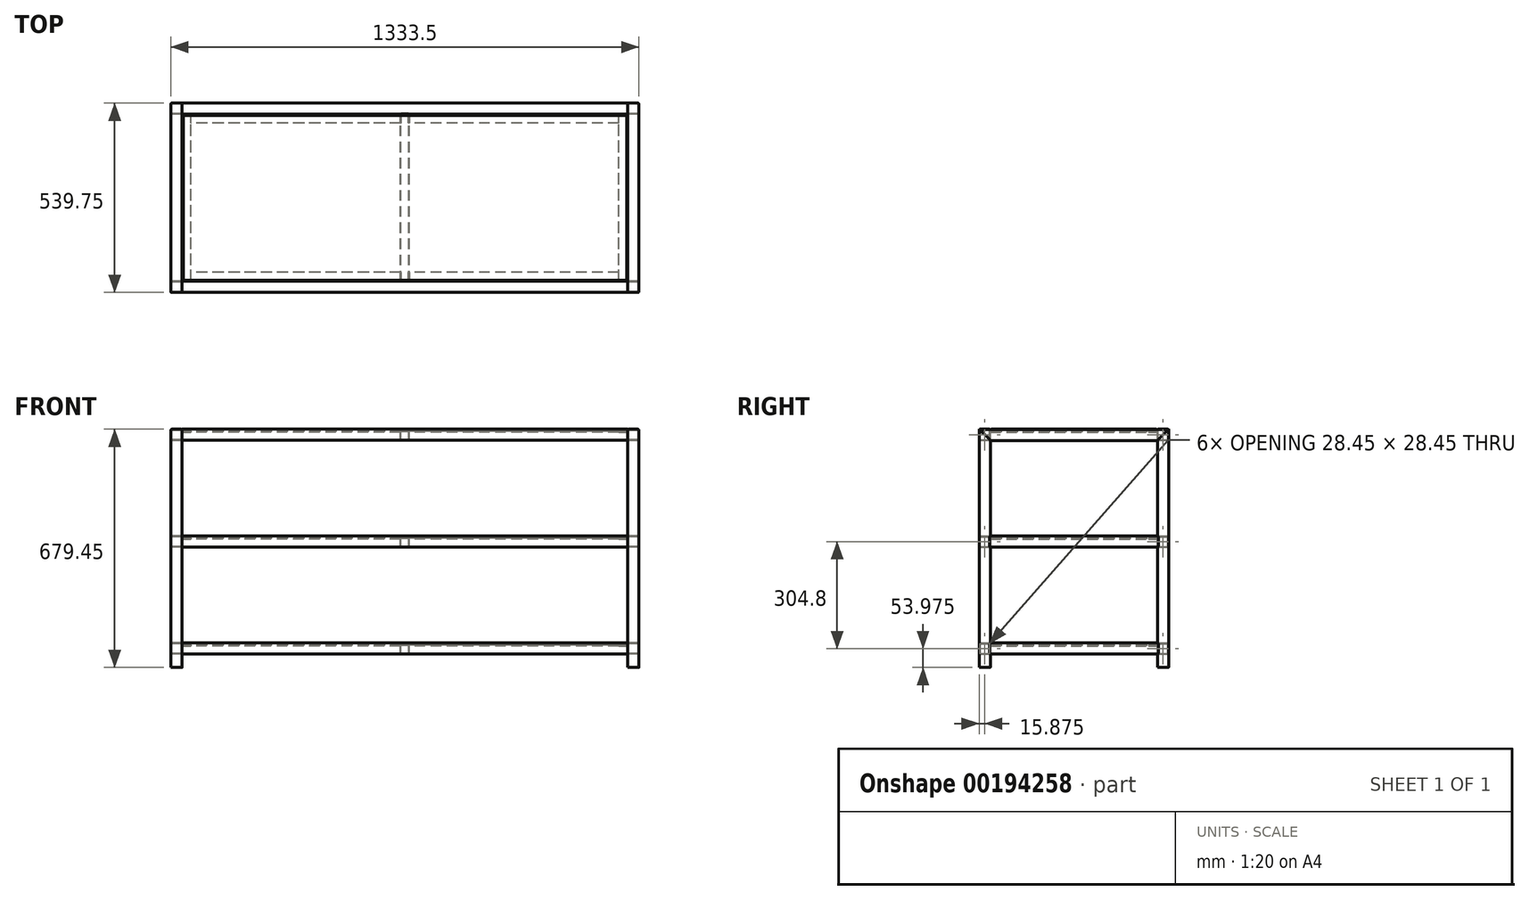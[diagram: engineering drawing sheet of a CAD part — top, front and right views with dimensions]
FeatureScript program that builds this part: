
annotation { "Feature Type Name" : "Feature", "Feature Type Description" : "" }
export const myFeature = defineFeature(function(context is Context, id is Id, definition is map)
    precondition{}
    {
        {
            var Q0;
            Q0=qCreatedBy(makeId("Right.planeOp"),FACE);
            var sketch = newSketch(context, id + "F0", { "sketchPlane" : qUnion([Q0])});
            skLineSegment(sketch, "E0.bottom", {"start": v(2.54, 0) * mm, "end": v(29.21, 0) * mm});
            skLineSegment(sketch, "E0.top", {"start": v(2.54, 31.75) * mm, "end": v(29.21, 31.75) * mm});
            skLineSegment(sketch, "E0.left", {"start": v(0, 2.54) * mm, "end": v(0, 29.21) * mm});
            skLineSegment(sketch, "E0.right", {"start": v(31.75, 2.54) * mm, "end": v(31.75, 29.21) * mm});
            skPoint(sketch, "E1.visualSharp", {"position": v(0, 31.75) * mm});
            skArc(sketch, "E1.filletArc", {"start": v(2.54, 31.75) * mm, "mid": v(0.74, 31) * mm, "end": v(0, 29.21) * mm});
            skPoint(sketch, "E2.visualSharp", {"position": v(31.75, 31.75) * mm});
            skArc(sketch, "E2.filletArc", {"start": v(31.75, 29.21) * mm, "mid": v(31, 31) * mm, "end": v(29.21, 31.75) * mm});
            skPoint(sketch, "E3.visualSharp", {"position": v(31.75, 0) * mm});
            skArc(sketch, "E3.filletArc", {"start": v(29.21, 0) * mm, "mid": v(31, 0.74) * mm, "end": v(31.75, 2.54) * mm});
            skPoint(sketch, "E4.visualSharp", {"position": v(0, 0) * mm});
            skArc(sketch, "E4.filletArc", {"start": v(0, 2.54) * mm, "mid": v(0.74, 0.74) * mm, "end": v(2.54, 0) * mm});
            skLineSegment(sketch, "E5.0", {"start": v(2.54, 30.1) * mm, "end": v(29.21, 30.1) * mm});
            skArc(sketch, "E5.1", {"start": v(2.54, 30.1) * mm, "mid": v(1.91, 29.84) * mm, "end": v(1.65, 29.21) * mm});
            skLineSegment(sketch, "E5.2", {"start": v(1.65, 2.54) * mm, "end": v(1.65, 29.21) * mm});
            skLineSegment(sketch, "E5.3", {"start": v(30.1, 2.54) * mm, "end": v(30.1, 29.21) * mm});
            skArc(sketch, "E5.4", {"start": v(29.21, 1.65) * mm, "mid": v(29.84, 1.91) * mm, "end": v(30.1, 2.54) * mm});
            skLineSegment(sketch, "E5.5", {"start": v(2.54, 1.65) * mm, "end": v(29.21, 1.65) * mm});
            skArc(sketch, "E5.6", {"start": v(1.65, 2.54) * mm, "mid": v(1.91, 1.91) * mm, "end": v(2.54, 1.65) * mm});
            skArc(sketch, "E6.0", {"start": v(30.1, 29.21) * mm, "mid": v(29.84, 29.84) * mm, "end": v(29.21, 30.1) * mm});
            skSolve(sketch);
        }
        {
            var Q0;
            Q0 = qSketchRegion(id + "F0", true);
            extrude(context, id + "F1", {"entities" : qUnion([Q0]), "depth" : 1270 * mm});
        }
        {
            var Q0;
            Q0=makeQuery(id+"F1.opExtrude","SWEPT_BODY",BODY,{"disambiguationData":[OSD([sQuery(id+"F0.wireOp",EDGE,"E0.bottom"),sQuery(id+"F0.wireOp",EDGE,"E0.top"),sQuery(id+"F0.wireOp",EDGE,"E0.left"),sQuery(id+"F0.wireOp",EDGE,"E0.right"),sQuery(id+"F0.wireOp",EDGE,"E1.filletArc"),sQuery(id+"F0.wireOp",EDGE,"E2.filletArc"),sQuery(id+"F0.wireOp",EDGE,"E3.filletArc"),sQuery(id+"F0.wireOp",EDGE,"E4.filletArc"),sQuery(id+"F0.wireOp",EDGE,"E5.0"),sQuery(id+"F0.wireOp",EDGE,"E5.1"),sQuery(id+"F0.wireOp",EDGE,"E5.2"),sQuery(id+"F0.wireOp",EDGE,"E5.3"),sQuery(id+"F0.wireOp",EDGE,"E5.4"),sQuery(id+"F0.wireOp",EDGE,"E5.5"),sQuery(id+"F0.wireOp",EDGE,"E5.6"),sQuery(id+"F0.wireOp",EDGE,"E6.0")])]});
            transform(context, id + "F2", {"entities" : qUnion([Q0]), "transformType" : TransformType.TRANSLATION_3D, "dx" : 0 * mm, "dy" : 0 * mm, "dz" : 304.8 * mm, "makeCopy" : true});
        }
        {
            var Q0;
            Q0=makeQuery(id+"F2.opPattern","COPY",BODY,{"derivedFrom":makeQuery(id+"F1.opExtrude","SWEPT_BODY",BODY,{"disambiguationData":[OSD([sQuery(id+"F0.wireOp",EDGE,"E0.bottom"),sQuery(id+"F0.wireOp",EDGE,"E0.top"),sQuery(id+"F0.wireOp",EDGE,"E0.left"),sQuery(id+"F0.wireOp",EDGE,"E0.right"),sQuery(id+"F0.wireOp",EDGE,"E1.filletArc"),sQuery(id+"F0.wireOp",EDGE,"E2.filletArc"),sQuery(id+"F0.wireOp",EDGE,"E3.filletArc"),sQuery(id+"F0.wireOp",EDGE,"E4.filletArc"),sQuery(id+"F0.wireOp",EDGE,"E5.0"),sQuery(id+"F0.wireOp",EDGE,"E5.1"),sQuery(id+"F0.wireOp",EDGE,"E5.2"),sQuery(id+"F0.wireOp",EDGE,"E5.3"),sQuery(id+"F0.wireOp",EDGE,"E5.4"),sQuery(id+"F0.wireOp",EDGE,"E5.5"),sQuery(id+"F0.wireOp",EDGE,"E5.6"),sQuery(id+"F0.wireOp",EDGE,"E6.0")])]}),"instanceName":"1"});
            transform(context, id + "F3", {"entities" : qUnion([Q0]), "transformType" : TransformType.TRANSLATION_3D, "dx" : 0 * mm, "dy" : 0 * mm, "dz" : 304.8 * mm, "makeCopy" : true});
        }
        {
            var Q0;
            Q0=makeQuery(id+"F1.opExtrude","SWEPT_BODY",BODY,{"disambiguationData":[OSD([sQuery(id+"F0.wireOp",EDGE,"E0.bottom"),sQuery(id+"F0.wireOp",EDGE,"E0.top"),sQuery(id+"F0.wireOp",EDGE,"E0.left"),sQuery(id+"F0.wireOp",EDGE,"E0.right"),sQuery(id+"F0.wireOp",EDGE,"E1.filletArc"),sQuery(id+"F0.wireOp",EDGE,"E2.filletArc"),sQuery(id+"F0.wireOp",EDGE,"E3.filletArc"),sQuery(id+"F0.wireOp",EDGE,"E4.filletArc"),sQuery(id+"F0.wireOp",EDGE,"E5.0"),sQuery(id+"F0.wireOp",EDGE,"E5.1"),sQuery(id+"F0.wireOp",EDGE,"E5.2"),sQuery(id+"F0.wireOp",EDGE,"E5.3"),sQuery(id+"F0.wireOp",EDGE,"E5.4"),sQuery(id+"F0.wireOp",EDGE,"E5.5"),sQuery(id+"F0.wireOp",EDGE,"E5.6"),sQuery(id+"F0.wireOp",EDGE,"E6.0")])]});
            transform(context, id + "F4", {"entities" : qUnion([Q0]), "transformType" : TransformType.TRANSLATION_3D, "dx" : 0 * mm, "dy" : 508 * mm, "dz" : 0 * mm, "makeCopy" : true});
        }
        {
            var Q0;
            Q0=makeQuery(id+"F4.opPattern","COPY",BODY,{"derivedFrom":makeQuery(id+"F1.opExtrude","SWEPT_BODY",BODY,{"disambiguationData":[OSD([sQuery(id+"F0.wireOp",EDGE,"E0.bottom"),sQuery(id+"F0.wireOp",EDGE,"E0.top"),sQuery(id+"F0.wireOp",EDGE,"E0.left"),sQuery(id+"F0.wireOp",EDGE,"E0.right"),sQuery(id+"F0.wireOp",EDGE,"E1.filletArc"),sQuery(id+"F0.wireOp",EDGE,"E2.filletArc"),sQuery(id+"F0.wireOp",EDGE,"E3.filletArc"),sQuery(id+"F0.wireOp",EDGE,"E4.filletArc"),sQuery(id+"F0.wireOp",EDGE,"E5.0"),sQuery(id+"F0.wireOp",EDGE,"E5.1"),sQuery(id+"F0.wireOp",EDGE,"E5.2"),sQuery(id+"F0.wireOp",EDGE,"E5.3"),sQuery(id+"F0.wireOp",EDGE,"E5.4"),sQuery(id+"F0.wireOp",EDGE,"E5.5"),sQuery(id+"F0.wireOp",EDGE,"E5.6"),sQuery(id+"F0.wireOp",EDGE,"E6.0")])]}),"instanceName":"1"});
            transform(context, id + "F5", {"entities" : qUnion([Q0]), "transformType" : TransformType.TRANSLATION_3D, "dx" : 0 * mm, "dy" : 0 * mm, "dz" : 304.8 * mm, "makeCopy" : true});
        }
        {
            var Q0;
            Q0=makeQuery(id+"F5.opPattern","COPY",BODY,{"derivedFrom":makeQuery(id+"F4.opPattern","COPY",BODY,{"derivedFrom":makeQuery(id+"F1.opExtrude","SWEPT_BODY",BODY,{"disambiguationData":[OSD([sQuery(id+"F0.wireOp",EDGE,"E0.bottom"),sQuery(id+"F0.wireOp",EDGE,"E0.top"),sQuery(id+"F0.wireOp",EDGE,"E0.left"),sQuery(id+"F0.wireOp",EDGE,"E0.right"),sQuery(id+"F0.wireOp",EDGE,"E1.filletArc"),sQuery(id+"F0.wireOp",EDGE,"E2.filletArc"),sQuery(id+"F0.wireOp",EDGE,"E3.filletArc"),sQuery(id+"F0.wireOp",EDGE,"E4.filletArc"),sQuery(id+"F0.wireOp",EDGE,"E5.0"),sQuery(id+"F0.wireOp",EDGE,"E5.1"),sQuery(id+"F0.wireOp",EDGE,"E5.2"),sQuery(id+"F0.wireOp",EDGE,"E5.3"),sQuery(id+"F0.wireOp",EDGE,"E5.4"),sQuery(id+"F0.wireOp",EDGE,"E5.5"),sQuery(id+"F0.wireOp",EDGE,"E5.6"),sQuery(id+"F0.wireOp",EDGE,"E6.0")])]}),"instanceName":"1"}),"instanceName":"1"});
            transform(context, id + "F6", {"entities" : qUnion([Q0]), "transformType" : TransformType.TRANSLATION_3D, "dx" : 0 * mm, "dy" : 0 * mm, "dz" : 304.8 * mm, "makeCopy" : true});
        }
        {
            var Q0;
            Q0=qCreatedBy(makeId("Top.planeOp"),FACE);
            var sketch = newSketch(context, id + "F7", { "sketchPlane" : qUnion([Q0])});
            skLineSegment(sketch, "E7.bottom", {"start": v(-2.54, 0) * mm, "end": v(-29.21, 0) * mm});
            skLineSegment(sketch, "E7.top", {"start": v(-2.54, 31.75) * mm, "end": v(-29.21, 31.75) * mm});
            skLineSegment(sketch, "E7.left", {"start": v(0, 2.54) * mm, "end": v(0, 29.21) * mm});
            skLineSegment(sketch, "E7.right", {"start": v(-31.75, 2.54) * mm, "end": v(-31.75, 29.21) * mm});
            skPoint(sketch, "E8.visualSharp", {"position": v(-31.75, 31.75) * mm});
            skArc(sketch, "E8.filletArc", {"start": v(-29.21, 31.75) * mm, "mid": v(-31, 31) * mm, "end": v(-31.75, 29.21) * mm});
            skPoint(sketch, "E9.visualSharp", {"position": v(0, 31.75) * mm});
            skArc(sketch, "E9.filletArc", {"start": v(0, 29.21) * mm, "mid": v(-0.74, 31) * mm, "end": v(-2.54, 31.75) * mm});
            skPoint(sketch, "E10.visualSharp", {"position": v(0, 0) * mm});
            skArc(sketch, "E10.filletArc", {"start": v(-2.54, 0) * mm, "mid": v(-0.74, 0.74) * mm, "end": v(0, 2.54) * mm});
            skPoint(sketch, "E11.visualSharp", {"position": v(-31.75, 0) * mm});
            skArc(sketch, "E11.filletArc", {"start": v(-31.75, 2.54) * mm, "mid": v(-31, 0.74) * mm, "end": v(-29.21, 0) * mm});
            skArc(sketch, "E12.0", {"start": v(-1.65, 29.21) * mm, "mid": v(-1.91, 29.84) * mm, "end": v(-2.54, 30.1) * mm});
            skLineSegment(sketch, "E12.1", {"start": v(-1.65, 2.54) * mm, "end": v(-1.65, 29.21) * mm});
            skLineSegment(sketch, "E12.2", {"start": v(-2.54, 30.1) * mm, "end": v(-29.21, 30.1) * mm});
            skArc(sketch, "E12.3", {"start": v(-2.54, 1.65) * mm, "mid": v(-1.91, 1.91) * mm, "end": v(-1.65, 2.54) * mm});
            skArc(sketch, "E12.4", {"start": v(-29.21, 30.1) * mm, "mid": v(-29.84, 29.84) * mm, "end": v(-30.1, 29.21) * mm});
            skLineSegment(sketch, "E12.5", {"start": v(-30.1, 2.54) * mm, "end": v(-30.1, 29.21) * mm});
            skArc(sketch, "E12.6", {"start": v(-30.1, 2.54) * mm, "mid": v(-29.84, 1.91) * mm, "end": v(-29.21, 1.65) * mm});
            skLineSegment(sketch, "E12.7", {"start": v(-2.54, 1.65) * mm, "end": v(-29.21, 1.65) * mm});
            skSolve(sketch);
        }
        {
            var Q0;
            Q0 = qSketchRegion(id + "F7", true);
            var Q1;
            Q1=makeQuery(id+"F3.opPattern","COPY",FACE,{"derivedFrom":makeQuery(id+"F2.opPattern","COPY",FACE,{"derivedFrom":makeQuery(id+"F1.opExtrude","SWEPT_FACE",FACE,{"disambiguationData":[OSD([sQuery(id+"F0.wireOp",EDGE,"E0.top")])]}),"instanceName":"1"}),"instanceName":"1"});
            extrude(context, id + "F8", {"entities" : qUnion([Q0]), "endBound" : BoundingType.UP_TO_SURFACE, "endBoundEntityFace" : qUnion([Q1]), "depth" : 25.4 * mm, "hasSecondDirection" : true, "secondDirectionOppositeDirection" : true, "secondDirectionDepth" : 38.1 * mm});
        }
        {
            var Q0;
            Q0=makeQuery(id+"F8.opExtrude","SWEPT_BODY",BODY,{"disambiguationData":[OSD([sQuery(id+"F7.wireOp",EDGE,"E7.bottom"),sQuery(id+"F7.wireOp",EDGE,"E7.top"),sQuery(id+"F7.wireOp",EDGE,"E7.left"),sQuery(id+"F7.wireOp",EDGE,"E7.right"),sQuery(id+"F7.wireOp",EDGE,"E8.filletArc"),sQuery(id+"F7.wireOp",EDGE,"E9.filletArc"),sQuery(id+"F7.wireOp",EDGE,"E10.filletArc"),sQuery(id+"F7.wireOp",EDGE,"E11.filletArc"),sQuery(id+"F7.wireOp",EDGE,"E12.0"),sQuery(id+"F7.wireOp",EDGE,"E12.1"),sQuery(id+"F7.wireOp",EDGE,"E12.2"),sQuery(id+"F7.wireOp",EDGE,"E12.3"),sQuery(id+"F7.wireOp",EDGE,"E12.4"),sQuery(id+"F7.wireOp",EDGE,"E12.5"),sQuery(id+"F7.wireOp",EDGE,"E12.6"),sQuery(id+"F7.wireOp",EDGE,"E12.7")])]});
            transform(context, id + "F9", {"entities" : qUnion([Q0]), "transformType" : TransformType.TRANSLATION_3D, "dx" : 1301.75 * mm, "dy" : 0 * mm, "dz" : 0 * mm, "makeCopy" : true});
        }
        {
            var Q0;
            Q0=makeQuery(id+"F8.opExtrude","SWEPT_FACE",FACE,{"disambiguationData":[OSD([sQuery(id+"F7.wireOp",EDGE,"E7.right")])]});
            var sketch = newSketch(context, id + "F10", { "sketchPlane" : qUnion([Q0])});
            skLineSegment(sketch, "E13.bottom", {"start": v(0, 641.35) * mm, "end": v(-31.75, 641.35) * mm});
            skLineSegment(sketch, "E13.right", {"start": v(-31.75, 641.35) * mm, "end": v(-31.75, 609.6) * mm});
            skLineSegment(sketch, "E14", {"start": v(-31.75, 609.6) * mm, "end": v(0, 641.35) * mm});
            skSolve(sketch);
        }
        {
            var Q0;
            Q0 = qSketchRegion(id + "F10", true);
            extrude(context, id + "F11", {"entities" : qUnion([Q0]), "operationType" : NewBodyOperationType.REMOVE, "oppositeDirection" : true, "depth" : 31.75 * mm});
        }
        {
            var Q0;
            Q0=makeQuery(id+"F9.opPattern","COPY",BODY,{"derivedFrom":makeQuery(id+"F8.opExtrude","SWEPT_BODY",BODY,{"disambiguationData":[OSD([sQuery(id+"F7.wireOp",EDGE,"E7.bottom"),sQuery(id+"F7.wireOp",EDGE,"E7.top"),sQuery(id+"F7.wireOp",EDGE,"E7.left"),sQuery(id+"F7.wireOp",EDGE,"E7.right"),sQuery(id+"F7.wireOp",EDGE,"E8.filletArc"),sQuery(id+"F7.wireOp",EDGE,"E9.filletArc"),sQuery(id+"F7.wireOp",EDGE,"E10.filletArc"),sQuery(id+"F7.wireOp",EDGE,"E11.filletArc"),sQuery(id+"F7.wireOp",EDGE,"E12.0"),sQuery(id+"F7.wireOp",EDGE,"E12.1"),sQuery(id+"F7.wireOp",EDGE,"E12.2"),sQuery(id+"F7.wireOp",EDGE,"E12.3"),sQuery(id+"F7.wireOp",EDGE,"E12.4"),sQuery(id+"F7.wireOp",EDGE,"E12.5"),sQuery(id+"F7.wireOp",EDGE,"E12.6"),sQuery(id+"F7.wireOp",EDGE,"E12.7")])]}),"instanceName":"1"});
            deleteBodies(context, id + "F12", {"entities" : qUnion([Q0])});
        }
        {
            var Q0;
            Q0=makeQuery(id+"F8.opExtrude","SWEPT_BODY",BODY,{"disambiguationData":[OSD([sQuery(id+"F7.wireOp",EDGE,"E7.bottom"),sQuery(id+"F7.wireOp",EDGE,"E7.top"),sQuery(id+"F7.wireOp",EDGE,"E7.left"),sQuery(id+"F7.wireOp",EDGE,"E7.right"),sQuery(id+"F7.wireOp",EDGE,"E8.filletArc"),sQuery(id+"F7.wireOp",EDGE,"E9.filletArc"),sQuery(id+"F7.wireOp",EDGE,"E10.filletArc"),sQuery(id+"F7.wireOp",EDGE,"E11.filletArc"),sQuery(id+"F7.wireOp",EDGE,"E12.0"),sQuery(id+"F7.wireOp",EDGE,"E12.1"),sQuery(id+"F7.wireOp",EDGE,"E12.2"),sQuery(id+"F7.wireOp",EDGE,"E12.3"),sQuery(id+"F7.wireOp",EDGE,"E12.4"),sQuery(id+"F7.wireOp",EDGE,"E12.5"),sQuery(id+"F7.wireOp",EDGE,"E12.6"),sQuery(id+"F7.wireOp",EDGE,"E12.7")])]});
            transform(context, id + "F13", {"entities" : qUnion([Q0]), "transformType" : TransformType.TRANSLATION_3D, "dx" : 1301.75 * mm, "dy" : 0 * mm, "dz" : 0 * mm, "makeCopy" : true});
        }
        {
            var Q0;
            Q0=makeQuery(id+"F8.opExtrude","SWEPT_BODY",BODY,{"disambiguationData":[OSD([sQuery(id+"F7.wireOp",EDGE,"E7.bottom"),sQuery(id+"F7.wireOp",EDGE,"E7.top"),sQuery(id+"F7.wireOp",EDGE,"E7.left"),sQuery(id+"F7.wireOp",EDGE,"E7.right"),sQuery(id+"F7.wireOp",EDGE,"E8.filletArc"),sQuery(id+"F7.wireOp",EDGE,"E9.filletArc"),sQuery(id+"F7.wireOp",EDGE,"E10.filletArc"),sQuery(id+"F7.wireOp",EDGE,"E11.filletArc"),sQuery(id+"F7.wireOp",EDGE,"E12.0"),sQuery(id+"F7.wireOp",EDGE,"E12.1"),sQuery(id+"F7.wireOp",EDGE,"E12.2"),sQuery(id+"F7.wireOp",EDGE,"E12.3"),sQuery(id+"F7.wireOp",EDGE,"E12.4"),sQuery(id+"F7.wireOp",EDGE,"E12.5"),sQuery(id+"F7.wireOp",EDGE,"E12.6"),sQuery(id+"F7.wireOp",EDGE,"E12.7")])]});
            transform(context, id + "F14", {"entities" : qUnion([Q0]), "transformType" : TransformType.TRANSLATION_3D, "dx" : 0 * mm, "dy" : 508 * mm, "dz" : 0 * mm, "makeCopy" : true});
        }
        {
            var Q0;
            Q0=makeQuery(id+"F14.opPattern","COPY",BODY,{"derivedFrom":makeQuery(id+"F8.opExtrude","SWEPT_BODY",BODY,{"disambiguationData":[OSD([sQuery(id+"F7.wireOp",EDGE,"E7.bottom"),sQuery(id+"F7.wireOp",EDGE,"E7.top"),sQuery(id+"F7.wireOp",EDGE,"E7.left"),sQuery(id+"F7.wireOp",EDGE,"E7.right"),sQuery(id+"F7.wireOp",EDGE,"E8.filletArc"),sQuery(id+"F7.wireOp",EDGE,"E9.filletArc"),sQuery(id+"F7.wireOp",EDGE,"E10.filletArc"),sQuery(id+"F7.wireOp",EDGE,"E11.filletArc"),sQuery(id+"F7.wireOp",EDGE,"E12.0"),sQuery(id+"F7.wireOp",EDGE,"E12.1"),sQuery(id+"F7.wireOp",EDGE,"E12.2"),sQuery(id+"F7.wireOp",EDGE,"E12.3"),sQuery(id+"F7.wireOp",EDGE,"E12.4"),sQuery(id+"F7.wireOp",EDGE,"E12.5"),sQuery(id+"F7.wireOp",EDGE,"E12.6"),sQuery(id+"F7.wireOp",EDGE,"E12.7")])]}),"instanceName":"1"});
            deleteBodies(context, id + "F15", {"entities" : qUnion([Q0])});
        }
        {
            var Q0;
            Q0=qCreatedBy(makeId("Top.planeOp"),FACE);
            var sketch = newSketch(context, id + "F16", { "sketchPlane" : qUnion([Q0])});
            skLineSegment(sketch, "E15.bottom", {"start": v(-2.54, 508) * mm, "end": v(-29.21, 508) * mm});
            skLineSegment(sketch, "E15.top", {"start": v(-2.54, 539.75) * mm, "end": v(-29.21, 539.75) * mm});
            skLineSegment(sketch, "E15.left", {"start": v(0, 510.54) * mm, "end": v(0, 537.2) * mm});
            skLineSegment(sketch, "E15.right", {"start": v(-31.75, 510.54) * mm, "end": v(-31.75, 537.2) * mm});
            skPoint(sketch, "E16.visualSharp", {"position": v(-31.75, 539.75) * mm});
            skArc(sketch, "E16.filletArc", {"start": v(-29.21, 539.75) * mm, "mid": v(-31, 539) * mm, "end": v(-31.75, 537.2) * mm});
            skPoint(sketch, "E17.visualSharp", {"position": v(0, 539.75) * mm});
            skArc(sketch, "E17.filletArc", {"start": v(0, 537.2) * mm, "mid": v(-0.74, 539) * mm, "end": v(-2.54, 539.75) * mm});
            skPoint(sketch, "E18.visualSharp", {"position": v(0, 508) * mm});
            skArc(sketch, "E18.filletArc", {"start": v(-2.54, 508) * mm, "mid": v(-0.74, 508.74) * mm, "end": v(0, 510.54) * mm});
            skPoint(sketch, "E19.visualSharp", {"position": v(-31.75, 508) * mm});
            skArc(sketch, "E19.filletArc", {"start": v(-31.75, 510.54) * mm, "mid": v(-31, 508.74) * mm, "end": v(-29.21, 508) * mm});
            skArc(sketch, "E20.0", {"start": v(-1.65, 537.2) * mm, "mid": v(-1.91, 537.84) * mm, "end": v(-2.54, 538.1) * mm});
            skLineSegment(sketch, "E20.1", {"start": v(-1.65, 510.54) * mm, "end": v(-1.65, 537.2) * mm});
            skLineSegment(sketch, "E20.2", {"start": v(-2.54, 538.1) * mm, "end": v(-29.21, 538.1) * mm});
            skArc(sketch, "E20.3", {"start": v(-2.54, 509.65) * mm, "mid": v(-1.91, 509.91) * mm, "end": v(-1.65, 510.54) * mm});
            skArc(sketch, "E20.4", {"start": v(-29.21, 538.1) * mm, "mid": v(-29.84, 537.84) * mm, "end": v(-30.1, 537.2) * mm});
            skLineSegment(sketch, "E20.5", {"start": v(-30.1, 510.54) * mm, "end": v(-30.1, 537.2) * mm});
            skArc(sketch, "E20.6", {"start": v(-30.1, 510.54) * mm, "mid": v(-29.84, 509.91) * mm, "end": v(-29.21, 509.65) * mm});
            skLineSegment(sketch, "E20.7", {"start": v(-2.54, 509.65) * mm, "end": v(-29.21, 509.65) * mm});
            skSolve(sketch);
        }
        {
            var Q0;
            Q0=makeQuery(id+"F16.imprint","IMPRINT",FACE,{"disambiguationData":[TD([[makeQuery(id+"F16.imprint","IMPRINT",EDGE,{"derivedFrom":sQuery(id+"F16.wireOp",EDGE,"E15.bottom")}),-1.0]])]});
            var Q1;
            Q1=makeQuery(id+"F6.opPattern","COPY",FACE,{"derivedFrom":makeQuery(id+"F5.opPattern","COPY",FACE,{"derivedFrom":makeQuery(id+"F4.opPattern","COPY",FACE,{"derivedFrom":makeQuery(id+"F1.opExtrude","SWEPT_FACE",FACE,{"disambiguationData":[OSD([sQuery(id+"F0.wireOp",EDGE,"E0.top")])]}),"instanceName":"1"}),"instanceName":"1"}),"instanceName":"1"});
            extrude(context, id + "F17", {"entities" : qUnion([Q0]), "endBound" : BoundingType.UP_TO_SURFACE, "endBoundEntityFace" : qUnion([Q1]), "depth" : 25.4 * mm, "hasSecondDirection" : true, "secondDirectionOppositeDirection" : true, "secondDirectionDepth" : 38.1 * mm});
        }
        {
            var Q0;
            Q0=makeQuery(id+"F17.opExtrude","SWEPT_FACE",FACE,{"disambiguationData":[OSD([sQuery(id+"F16.wireOp",EDGE,"E15.right")])]});
            var sketch = newSketch(context, id + "F18", { "sketchPlane" : qUnion([Q0])});
            skLineSegment(sketch, "E21.bottom", {"start": v(-508, 641.35) * mm, "end": v(-539.75, 641.35) * mm});
            skLineSegment(sketch, "E21.left", {"start": v(-508, 641.35) * mm, "end": v(-508, 609.6) * mm});
            skLineSegment(sketch, "E22", {"start": v(-539.75, 641.35) * mm, "end": v(-508, 609.6) * mm});
            skSolve(sketch);
        }
        {
            var Q0;
            Q0 = qSketchRegion(id + "F18", true);
            extrude(context, id + "F19", {"entities" : qUnion([Q0]), "operationType" : NewBodyOperationType.REMOVE, "oppositeDirection" : true, "depth" : 31.75 * mm});
        }
        {
            var Q0;
            Q0=makeQuery(id+"F17.opExtrude","SWEPT_BODY",BODY,{"disambiguationData":[OSD([sQuery(id+"F16.wireOp",EDGE,"E15.bottom"),sQuery(id+"F16.wireOp",EDGE,"E15.top"),sQuery(id+"F16.wireOp",EDGE,"E15.left"),sQuery(id+"F16.wireOp",EDGE,"E15.right"),sQuery(id+"F16.wireOp",EDGE,"E16.filletArc"),sQuery(id+"F16.wireOp",EDGE,"E17.filletArc"),sQuery(id+"F16.wireOp",EDGE,"E18.filletArc"),sQuery(id+"F16.wireOp",EDGE,"E19.filletArc"),sQuery(id+"F16.wireOp",EDGE,"E20.0"),sQuery(id+"F16.wireOp",EDGE,"E20.1"),sQuery(id+"F16.wireOp",EDGE,"E20.2"),sQuery(id+"F16.wireOp",EDGE,"E20.3"),sQuery(id+"F16.wireOp",EDGE,"E20.4"),sQuery(id+"F16.wireOp",EDGE,"E20.5"),sQuery(id+"F16.wireOp",EDGE,"E20.6"),sQuery(id+"F16.wireOp",EDGE,"E20.7")])]});
            transform(context, id + "F20", {"entities" : qUnion([Q0]), "transformType" : TransformType.TRANSLATION_3D, "dx" : 1301.75 * mm, "dy" : 0 * mm, "dz" : 0 * mm, "makeCopy" : true});
        }
        {
            var Q0;
            Q0=qCreatedBy(makeId("Front.planeOp"),FACE);
            cPlane(context, id + "F21", {"entities" : qUnion([Q0]), "cplaneType" : CPlaneType.OFFSET, "offset" : 279.4 * mm, "oppositeDirection" : true, "width" : 152.4 * mm, "height" : 152.4 * mm});
        }
        {
            var Q0;
            Q0=qCreatedBy(id+"F21.planeOp",FACE);
            var sketch = newSketch(context, id + "F22", { "sketchPlane" : qUnion([Q0])});
            skLineSegment(sketch, "E23.0", {"start": v(-2.54, 641.35) * mm, "end": v(-29.2, 641.35) * mm});
            skPoint(sketch, "E24.0", {"position": v(-31.75, 625.47) * mm});
            skLineSegment(sketch, "E25.bottom", {"start": v(-2.54, 641.26) * mm, "end": v(-29.21, 641.26) * mm});
            skLineSegment(sketch, "E25.top", {"start": v(-2.54, 609.51) * mm, "end": v(-29.21, 609.51) * mm});
            skLineSegment(sketch, "E25.left", {"start": v(0, 638.72) * mm, "end": v(0, 612.05) * mm});
            skLineSegment(sketch, "E25.right", {"start": v(-31.75, 638.72) * mm, "end": v(-31.75, 612.05) * mm});
            skPoint(sketch, "E26.visualSharp", {"position": v(0, 641.26) * mm});
            skArc(sketch, "E26.filletArc", {"start": v(0, 638.72) * mm, "mid": v(-0.74, 640.52) * mm, "end": v(-2.54, 641.26) * mm});
            skPoint(sketch, "E27.visualSharp", {"position": v(0, 609.51) * mm});
            skArc(sketch, "E27.filletArc", {"start": v(-2.54, 609.51) * mm, "mid": v(-0.74, 610.26) * mm, "end": v(0, 612.05) * mm});
            skPoint(sketch, "E28.visualSharp", {"position": v(-31.75, 609.51) * mm});
            skArc(sketch, "E28.filletArc", {"start": v(-31.75, 612.05) * mm, "mid": v(-31, 610.26) * mm, "end": v(-29.21, 609.51) * mm});
            skPoint(sketch, "E29.visualSharp", {"position": v(-31.75, 641.26) * mm});
            skArc(sketch, "E29.filletArc", {"start": v(-29.21, 641.26) * mm, "mid": v(-31, 640.52) * mm, "end": v(-31.75, 638.72) * mm});
            skLineSegment(sketch, "E30.0", {"start": v(-1.65, 638.72) * mm, "end": v(-1.65, 612.05) * mm});
            skArc(sketch, "E30.1", {"start": v(-2.54, 611.16) * mm, "mid": v(-1.91, 611.42) * mm, "end": v(-1.65, 612.05) * mm});
            skArc(sketch, "E30.2", {"start": v(-1.65, 638.72) * mm, "mid": v(-1.91, 639.35) * mm, "end": v(-2.54, 639.61) * mm});
            skLineSegment(sketch, "E30.3", {"start": v(-2.54, 611.16) * mm, "end": v(-29.2, 611.16) * mm});
            skLineSegment(sketch, "E30.4", {"start": v(-2.54, 639.61) * mm, "end": v(-29.21, 639.61) * mm});
            skArc(sketch, "E30.5", {"start": v(-29.21, 639.61) * mm, "mid": v(-29.84, 639.35) * mm, "end": v(-30.1, 638.72) * mm});
            skLineSegment(sketch, "E30.6", {"start": v(-30.1, 638.72) * mm, "end": v(-30.1, 612.05) * mm});
            skArc(sketch, "E30.7", {"start": v(-30.1, 612.05) * mm, "mid": v(-29.84, 611.42) * mm, "end": v(-29.2, 611.16) * mm});
            skSolve(sketch);
        }
        {
            var Q0;
            Q0 = qSketchRegion(id + "F22", true);
            var Q1;
            Q1=makeQuery(id+"F8.opExtrude","SWEPT_BODY",BODY,{"disambiguationData":[OSD([sQuery(id+"F7.wireOp",EDGE,"E7.bottom"),sQuery(id+"F7.wireOp",EDGE,"E7.top"),sQuery(id+"F7.wireOp",EDGE,"E7.left"),sQuery(id+"F7.wireOp",EDGE,"E7.right"),sQuery(id+"F7.wireOp",EDGE,"E8.filletArc"),sQuery(id+"F7.wireOp",EDGE,"E9.filletArc"),sQuery(id+"F7.wireOp",EDGE,"E10.filletArc"),sQuery(id+"F7.wireOp",EDGE,"E11.filletArc"),sQuery(id+"F7.wireOp",EDGE,"E12.0"),sQuery(id+"F7.wireOp",EDGE,"E12.1"),sQuery(id+"F7.wireOp",EDGE,"E12.2"),sQuery(id+"F7.wireOp",EDGE,"E12.3"),sQuery(id+"F7.wireOp",EDGE,"E12.4"),sQuery(id+"F7.wireOp",EDGE,"E12.5"),sQuery(id+"F7.wireOp",EDGE,"E12.6"),sQuery(id+"F7.wireOp",EDGE,"E12.7")])]});
            var Q2;
            Q2=makeQuery(id+"F17.opExtrude","SWEPT_BODY",BODY,{"disambiguationData":[OSD([sQuery(id+"F16.wireOp",EDGE,"E15.bottom"),sQuery(id+"F16.wireOp",EDGE,"E15.top"),sQuery(id+"F16.wireOp",EDGE,"E15.left"),sQuery(id+"F16.wireOp",EDGE,"E15.right"),sQuery(id+"F16.wireOp",EDGE,"E16.filletArc"),sQuery(id+"F16.wireOp",EDGE,"E17.filletArc"),sQuery(id+"F16.wireOp",EDGE,"E18.filletArc"),sQuery(id+"F16.wireOp",EDGE,"E19.filletArc"),sQuery(id+"F16.wireOp",EDGE,"E20.0"),sQuery(id+"F16.wireOp",EDGE,"E20.1"),sQuery(id+"F16.wireOp",EDGE,"E20.2"),sQuery(id+"F16.wireOp",EDGE,"E20.3"),sQuery(id+"F16.wireOp",EDGE,"E20.4"),sQuery(id+"F16.wireOp",EDGE,"E20.5"),sQuery(id+"F16.wireOp",EDGE,"E20.6"),sQuery(id+"F16.wireOp",EDGE,"E20.7")])]});
            extrude(context, id + "F23", {"entities" : qUnion([Q0]), "endBound" : BoundingType.UP_TO_BODY, "endBoundEntityBody" : qUnion([Q1]), "depth" : 25.4 * mm, "hasSecondDirection" : true, "secondDirectionBound" : SecondDirectionBoundingType.UP_TO_BODY, "secondDirectionOppositeDirection" : true, "secondDirectionBoundEntityBody" : qUnion([Q2]), "secondDirectionDepth" : 25.4 * mm});
        }
        {
            var Q0;
            Q0=makeQuery(id+"F23.opExtrude","SWEPT_BODY",BODY,{"disambiguationData":[OSD([sQuery(id+"F22.wireOp",EDGE,"E25.bottom"),sQuery(id+"F22.wireOp",EDGE,"E25.top"),sQuery(id+"F22.wireOp",EDGE,"E25.left"),sQuery(id+"F22.wireOp",EDGE,"E25.right"),sQuery(id+"F22.wireOp",EDGE,"E26.filletArc"),sQuery(id+"F22.wireOp",EDGE,"E27.filletArc"),sQuery(id+"F22.wireOp",EDGE,"E28.filletArc"),sQuery(id+"F22.wireOp",EDGE,"E29.filletArc"),sQuery(id+"F22.wireOp",EDGE,"E30.0"),sQuery(id+"F22.wireOp",EDGE,"E30.1"),sQuery(id+"F22.wireOp",EDGE,"E30.2"),sQuery(id+"F22.wireOp",EDGE,"E30.3"),sQuery(id+"F22.wireOp",EDGE,"E30.4"),sQuery(id+"F22.wireOp",EDGE,"E30.5"),sQuery(id+"F22.wireOp",EDGE,"E30.6"),sQuery(id+"F22.wireOp",EDGE,"E30.7")])]});
            transform(context, id + "F24", {"entities" : qUnion([Q0]), "transformType" : TransformType.TRANSLATION_3D, "dx" : 1301.75 * mm, "dy" : 0 * mm, "dz" : 0 * mm, "makeCopy" : true});
        }
        {
            var Q0;
            Q0=qCreatedBy(id+"F21.planeOp",FACE);
            var sketch = newSketch(context, id + "F25", { "sketchPlane" : qUnion([Q0])});
            skLineSegment(sketch, "E31.bottom", {"start": v(-2.54, 0) * mm, "end": v(-29.21, 0) * mm});
            skLineSegment(sketch, "E31.top", {"start": v(-2.54, 31.75) * mm, "end": v(-29.21, 31.75) * mm});
            skLineSegment(sketch, "E31.left", {"start": v(0, 2.54) * mm, "end": v(0, 29.21) * mm});
            skLineSegment(sketch, "E31.right", {"start": v(-31.75, 2.54) * mm, "end": v(-31.75, 29.21) * mm});
            skPoint(sketch, "E32.visualSharp", {"position": v(-31.75, 31.75) * mm});
            skArc(sketch, "E32.filletArc", {"start": v(-29.21, 31.75) * mm, "mid": v(-31, 31) * mm, "end": v(-31.75, 29.21) * mm});
            skPoint(sketch, "E33.visualSharp", {"position": v(0, 31.75) * mm});
            skArc(sketch, "E33.filletArc", {"start": v(0, 29.21) * mm, "mid": v(-0.74, 31) * mm, "end": v(-2.54, 31.75) * mm});
            skPoint(sketch, "E34.visualSharp", {"position": v(0, 0) * mm});
            skArc(sketch, "E34.filletArc", {"start": v(-2.54, 0) * mm, "mid": v(-0.74, 0.74) * mm, "end": v(0, 2.54) * mm});
            skPoint(sketch, "E35.visualSharp", {"position": v(-31.75, 0) * mm});
            skArc(sketch, "E35.filletArc", {"start": v(-31.75, 2.54) * mm, "mid": v(-31, 0.74) * mm, "end": v(-29.21, 0) * mm});
            skArc(sketch, "E36.0", {"start": v(-1.65, 29.21) * mm, "mid": v(-1.91, 29.84) * mm, "end": v(-2.54, 30.1) * mm});
            skLineSegment(sketch, "E36.1", {"start": v(-1.65, 2.54) * mm, "end": v(-1.65, 29.21) * mm});
            skLineSegment(sketch, "E36.2", {"start": v(-2.54, 30.1) * mm, "end": v(-29.21, 30.1) * mm});
            skArc(sketch, "E36.3", {"start": v(-2.54, 1.65) * mm, "mid": v(-1.91, 1.91) * mm, "end": v(-1.65, 2.54) * mm});
            skArc(sketch, "E36.4", {"start": v(-29.21, 30.1) * mm, "mid": v(-29.84, 29.84) * mm, "end": v(-30.1, 29.21) * mm});
            skLineSegment(sketch, "E36.5", {"start": v(-30.1, 2.54) * mm, "end": v(-30.1, 29.21) * mm});
            skArc(sketch, "E36.6", {"start": v(-30.1, 2.54) * mm, "mid": v(-29.84, 1.91) * mm, "end": v(-29.21, 1.65) * mm});
            skLineSegment(sketch, "E36.7", {"start": v(-2.54, 1.65) * mm, "end": v(-29.21, 1.65) * mm});
            skSolve(sketch);
        }
        {
            var Q0;
            Q0 = qSketchRegion(id + "F25", true);
            var Q1;
            Q1=makeQuery(id+"F8.opExtrude","SWEPT_BODY",BODY,{"disambiguationData":[OSD([sQuery(id+"F7.wireOp",EDGE,"E7.bottom"),sQuery(id+"F7.wireOp",EDGE,"E7.top"),sQuery(id+"F7.wireOp",EDGE,"E7.left"),sQuery(id+"F7.wireOp",EDGE,"E7.right"),sQuery(id+"F7.wireOp",EDGE,"E8.filletArc"),sQuery(id+"F7.wireOp",EDGE,"E9.filletArc"),sQuery(id+"F7.wireOp",EDGE,"E10.filletArc"),sQuery(id+"F7.wireOp",EDGE,"E11.filletArc"),sQuery(id+"F7.wireOp",EDGE,"E12.0"),sQuery(id+"F7.wireOp",EDGE,"E12.1"),sQuery(id+"F7.wireOp",EDGE,"E12.2"),sQuery(id+"F7.wireOp",EDGE,"E12.3"),sQuery(id+"F7.wireOp",EDGE,"E12.4"),sQuery(id+"F7.wireOp",EDGE,"E12.5"),sQuery(id+"F7.wireOp",EDGE,"E12.6"),sQuery(id+"F7.wireOp",EDGE,"E12.7")])]});
            var Q2;
            Q2=makeQuery(id+"F17.opExtrude","SWEPT_BODY",BODY,{"disambiguationData":[OSD([sQuery(id+"F16.wireOp",EDGE,"E15.bottom"),sQuery(id+"F16.wireOp",EDGE,"E15.top"),sQuery(id+"F16.wireOp",EDGE,"E15.left"),sQuery(id+"F16.wireOp",EDGE,"E15.right"),sQuery(id+"F16.wireOp",EDGE,"E16.filletArc"),sQuery(id+"F16.wireOp",EDGE,"E17.filletArc"),sQuery(id+"F16.wireOp",EDGE,"E18.filletArc"),sQuery(id+"F16.wireOp",EDGE,"E19.filletArc"),sQuery(id+"F16.wireOp",EDGE,"E20.0"),sQuery(id+"F16.wireOp",EDGE,"E20.1"),sQuery(id+"F16.wireOp",EDGE,"E20.2"),sQuery(id+"F16.wireOp",EDGE,"E20.3"),sQuery(id+"F16.wireOp",EDGE,"E20.4"),sQuery(id+"F16.wireOp",EDGE,"E20.5"),sQuery(id+"F16.wireOp",EDGE,"E20.6"),sQuery(id+"F16.wireOp",EDGE,"E20.7")])]});
            extrude(context, id + "F26", {"entities" : qUnion([Q0]), "endBound" : BoundingType.UP_TO_BODY, "endBoundEntityBody" : qUnion([Q1]), "depth" : 25.4 * mm, "hasSecondDirection" : true, "secondDirectionBound" : SecondDirectionBoundingType.UP_TO_BODY, "secondDirectionOppositeDirection" : true, "secondDirectionBoundEntityBody" : qUnion([Q2]), "secondDirectionDepth" : 25.4 * mm});
        }
        {
            var Q0;
            Q0=makeQuery(id+"F26.opExtrude","SWEPT_BODY",BODY,{"disambiguationData":[OSD([sQuery(id+"F25.wireOp",EDGE,"E31.bottom"),sQuery(id+"F25.wireOp",EDGE,"E31.top"),sQuery(id+"F25.wireOp",EDGE,"E31.left"),sQuery(id+"F25.wireOp",EDGE,"E31.right"),sQuery(id+"F25.wireOp",EDGE,"E32.filletArc"),sQuery(id+"F25.wireOp",EDGE,"E33.filletArc"),sQuery(id+"F25.wireOp",EDGE,"E34.filletArc"),sQuery(id+"F25.wireOp",EDGE,"E35.filletArc"),sQuery(id+"F25.wireOp",EDGE,"E36.0"),sQuery(id+"F25.wireOp",EDGE,"E36.1"),sQuery(id+"F25.wireOp",EDGE,"E36.2"),sQuery(id+"F25.wireOp",EDGE,"E36.3"),sQuery(id+"F25.wireOp",EDGE,"E36.4"),sQuery(id+"F25.wireOp",EDGE,"E36.5"),sQuery(id+"F25.wireOp",EDGE,"E36.6"),sQuery(id+"F25.wireOp",EDGE,"E36.7")])]});
            transform(context, id + "F27", {"entities" : qUnion([Q0]), "transformType" : TransformType.TRANSLATION_3D, "dx" : 1301.75 * mm, "dy" : 0 * mm, "dz" : 0 * mm, "makeCopy" : true});
        }
        {
            var Q0;
            Q0=makeQuery(id+"F26.opExtrude","SWEPT_BODY",BODY,{"disambiguationData":[OSD([sQuery(id+"F25.wireOp",EDGE,"E31.bottom"),sQuery(id+"F25.wireOp",EDGE,"E31.top"),sQuery(id+"F25.wireOp",EDGE,"E31.left"),sQuery(id+"F25.wireOp",EDGE,"E31.right"),sQuery(id+"F25.wireOp",EDGE,"E32.filletArc"),sQuery(id+"F25.wireOp",EDGE,"E33.filletArc"),sQuery(id+"F25.wireOp",EDGE,"E34.filletArc"),sQuery(id+"F25.wireOp",EDGE,"E35.filletArc"),sQuery(id+"F25.wireOp",EDGE,"E36.0"),sQuery(id+"F25.wireOp",EDGE,"E36.1"),sQuery(id+"F25.wireOp",EDGE,"E36.2"),sQuery(id+"F25.wireOp",EDGE,"E36.3"),sQuery(id+"F25.wireOp",EDGE,"E36.4"),sQuery(id+"F25.wireOp",EDGE,"E36.5"),sQuery(id+"F25.wireOp",EDGE,"E36.6"),sQuery(id+"F25.wireOp",EDGE,"E36.7")])]});
            transform(context, id + "F28", {"entities" : qUnion([Q0]), "transformType" : TransformType.TRANSLATION_3D, "dx" : 0 * mm, "dy" : 0 * mm, "dz" : 304.8 * mm, "makeCopy" : true});
        }
        {
            var Q0;
            Q0=makeQuery(id+"F27.opPattern","COPY",BODY,{"derivedFrom":makeQuery(id+"F26.opExtrude","SWEPT_BODY",BODY,{"disambiguationData":[OSD([sQuery(id+"F25.wireOp",EDGE,"E31.bottom"),sQuery(id+"F25.wireOp",EDGE,"E31.top"),sQuery(id+"F25.wireOp",EDGE,"E31.left"),sQuery(id+"F25.wireOp",EDGE,"E31.right"),sQuery(id+"F25.wireOp",EDGE,"E32.filletArc"),sQuery(id+"F25.wireOp",EDGE,"E33.filletArc"),sQuery(id+"F25.wireOp",EDGE,"E34.filletArc"),sQuery(id+"F25.wireOp",EDGE,"E35.filletArc"),sQuery(id+"F25.wireOp",EDGE,"E36.0"),sQuery(id+"F25.wireOp",EDGE,"E36.1"),sQuery(id+"F25.wireOp",EDGE,"E36.2"),sQuery(id+"F25.wireOp",EDGE,"E36.3"),sQuery(id+"F25.wireOp",EDGE,"E36.4"),sQuery(id+"F25.wireOp",EDGE,"E36.5"),sQuery(id+"F25.wireOp",EDGE,"E36.6"),sQuery(id+"F25.wireOp",EDGE,"E36.7")])]}),"instanceName":"1"});
            transform(context, id + "F29", {"entities" : qUnion([Q0]), "transformType" : TransformType.TRANSLATION_3D, "dx" : 0 * mm, "dy" : 0 * mm, "dz" : 304.8 * mm, "makeCopy" : true});
        }
        {
            var Q0;
            Q0=qCreatedBy(id+"F21.planeOp",FACE);
            var sketch = newSketch(context, id + "F30", { "sketchPlane" : qUnion([Q0])});
            skLineSegment(sketch, "E37.bottom", {"start": v(0, 25.4) * mm, "end": v(25.4, 25.4) * mm});
            skLineSegment(sketch, "E37.top", {"start": v(0, 22.86) * mm, "end": v(25.4, 22.86) * mm});
            skLineSegment(sketch, "E37.left", {"start": v(0, 25.4) * mm, "end": v(0, 22.86) * mm});
            skLineSegment(sketch, "E37.right", {"start": v(25.4, 25.4) * mm, "end": v(25.4, 22.86) * mm});
            skSolve(sketch);
        }
        {
            var Q0;
            Q0 = qSketchRegion(id + "F30", true);
            var Q1;
            Q1=makeQuery(id+"F1.opExtrude","SWEPT_BODY",BODY,{"disambiguationData":[OSD([sQuery(id+"F0.wireOp",EDGE,"E0.bottom"),sQuery(id+"F0.wireOp",EDGE,"E0.top"),sQuery(id+"F0.wireOp",EDGE,"E0.left"),sQuery(id+"F0.wireOp",EDGE,"E0.right"),sQuery(id+"F0.wireOp",EDGE,"E1.filletArc"),sQuery(id+"F0.wireOp",EDGE,"E2.filletArc"),sQuery(id+"F0.wireOp",EDGE,"E3.filletArc"),sQuery(id+"F0.wireOp",EDGE,"E4.filletArc"),sQuery(id+"F0.wireOp",EDGE,"E5.0"),sQuery(id+"F0.wireOp",EDGE,"E5.1"),sQuery(id+"F0.wireOp",EDGE,"E5.2"),sQuery(id+"F0.wireOp",EDGE,"E5.3"),sQuery(id+"F0.wireOp",EDGE,"E5.4"),sQuery(id+"F0.wireOp",EDGE,"E5.5"),sQuery(id+"F0.wireOp",EDGE,"E5.6"),sQuery(id+"F0.wireOp",EDGE,"E6.0")])]});
            var Q2;
            Q2=makeQuery(id+"F4.opPattern","COPY",BODY,{"derivedFrom":makeQuery(id+"F1.opExtrude","SWEPT_BODY",BODY,{"disambiguationData":[OSD([sQuery(id+"F0.wireOp",EDGE,"E0.bottom"),sQuery(id+"F0.wireOp",EDGE,"E0.top"),sQuery(id+"F0.wireOp",EDGE,"E0.left"),sQuery(id+"F0.wireOp",EDGE,"E0.right"),sQuery(id+"F0.wireOp",EDGE,"E1.filletArc"),sQuery(id+"F0.wireOp",EDGE,"E2.filletArc"),sQuery(id+"F0.wireOp",EDGE,"E3.filletArc"),sQuery(id+"F0.wireOp",EDGE,"E4.filletArc"),sQuery(id+"F0.wireOp",EDGE,"E5.0"),sQuery(id+"F0.wireOp",EDGE,"E5.1"),sQuery(id+"F0.wireOp",EDGE,"E5.2"),sQuery(id+"F0.wireOp",EDGE,"E5.3"),sQuery(id+"F0.wireOp",EDGE,"E5.4"),sQuery(id+"F0.wireOp",EDGE,"E5.5"),sQuery(id+"F0.wireOp",EDGE,"E5.6"),sQuery(id+"F0.wireOp",EDGE,"E6.0")])]}),"instanceName":"1"});
            extrude(context, id + "F31", {"entities" : qUnion([Q0]), "endBound" : BoundingType.UP_TO_BODY, "endBoundEntityBody" : qUnion([Q1]), "depth" : 25.4 * mm, "hasSecondDirection" : true, "secondDirectionBound" : SecondDirectionBoundingType.UP_TO_BODY, "secondDirectionOppositeDirection" : true, "secondDirectionBoundEntityBody" : qUnion([Q2]), "secondDirectionDepth" : 25.4 * mm});
        }
        {
            var Q0;
            Q0=makeQuery(id+"F31.opExtrude","SWEPT_BODY",BODY,{"disambiguationData":[OSD([sQuery(id+"F30.wireOp",EDGE,"E37.bottom"),sQuery(id+"F30.wireOp",EDGE,"E37.top"),sQuery(id+"F30.wireOp",EDGE,"E37.left"),sQuery(id+"F30.wireOp",EDGE,"E37.right")])]});
            transform(context, id + "F32", {"entities" : qUnion([Q0]), "transformType" : TransformType.TRANSLATION_3D, "dx" : 1244.6 * mm, "dy" : 0 * mm, "dz" : 0 * mm, "makeCopy" : true});
        }
        {
            var Q0;
            Q0=makeQuery(id+"F31.opExtrude","SWEPT_BODY",BODY,{"disambiguationData":[OSD([sQuery(id+"F30.wireOp",EDGE,"E37.bottom"),sQuery(id+"F30.wireOp",EDGE,"E37.top"),sQuery(id+"F30.wireOp",EDGE,"E37.left"),sQuery(id+"F30.wireOp",EDGE,"E37.right")])]});
            transform(context, id + "F33", {"entities" : qUnion([Q0]), "transformType" : TransformType.TRANSLATION_3D, "dx" : 0 * mm, "dy" : 0 * mm, "dz" : 304.8 * mm, "makeCopy" : true});
        }
        {
            var Q0;
            Q0=makeQuery(id+"F33.opPattern","COPY",BODY,{"derivedFrom":makeQuery(id+"F31.opExtrude","SWEPT_BODY",BODY,{"disambiguationData":[OSD([sQuery(id+"F30.wireOp",EDGE,"E37.bottom"),sQuery(id+"F30.wireOp",EDGE,"E37.top"),sQuery(id+"F30.wireOp",EDGE,"E37.left"),sQuery(id+"F30.wireOp",EDGE,"E37.right")])]}),"instanceName":"1"});
            transform(context, id + "F34", {"entities" : qUnion([Q0]), "transformType" : TransformType.TRANSLATION_3D, "dx" : 0 * mm, "dy" : 0 * mm, "dz" : 304.8 * mm, "makeCopy" : true});
        }
        {
            var Q0;
            Q0=makeQuery(id+"F32.opPattern","COPY",BODY,{"derivedFrom":makeQuery(id+"F31.opExtrude","SWEPT_BODY",BODY,{"disambiguationData":[OSD([sQuery(id+"F30.wireOp",EDGE,"E37.bottom"),sQuery(id+"F30.wireOp",EDGE,"E37.top"),sQuery(id+"F30.wireOp",EDGE,"E37.left"),sQuery(id+"F30.wireOp",EDGE,"E37.right")])]}),"instanceName":"1"});
            transform(context, id + "F35", {"entities" : qUnion([Q0]), "transformType" : TransformType.TRANSLATION_3D, "dx" : 0 * mm, "dy" : 0 * mm, "dz" : 304.8 * mm, "makeCopy" : true});
        }
        {
            var Q0;
            Q0=makeQuery(id+"F35.opPattern","COPY",BODY,{"derivedFrom":makeQuery(id+"F32.opPattern","COPY",BODY,{"derivedFrom":makeQuery(id+"F31.opExtrude","SWEPT_BODY",BODY,{"disambiguationData":[OSD([sQuery(id+"F30.wireOp",EDGE,"E37.bottom"),sQuery(id+"F30.wireOp",EDGE,"E37.top"),sQuery(id+"F30.wireOp",EDGE,"E37.left"),sQuery(id+"F30.wireOp",EDGE,"E37.right")])]}),"instanceName":"1"}),"instanceName":"1"});
            transform(context, id + "F36", {"entities" : qUnion([Q0]), "transformType" : TransformType.TRANSLATION_3D, "dx" : 0 * mm, "dy" : 0 * mm, "dz" : 304.8 * mm, "makeCopy" : true});
        }
        {
            var Q0;
            Q0=qCreatedBy(makeId("Right.planeOp"),FACE);
            cPlane(context, id + "F37", {"entities" : qUnion([Q0]), "cplaneType" : CPlaneType.OFFSET, "offset" : 635 * mm, "width" : 152.4 * mm, "height" : 152.4 * mm});
        }
        {
            var Q0;
            Q0=qCreatedBy(makeId("Front.planeOp"),FACE);
            var sketch = newSketch(context, id + "F38", { "sketchPlane" : qUnion([Q0])});
            skLineSegment(sketch, "E38.bottom", {"start": v(645.16, 0) * mm, "end": v(624.84, 0) * mm});
            skLineSegment(sketch, "E38.top", {"start": v(645.16, 25.4) * mm, "end": v(624.84, 25.4) * mm});
            skLineSegment(sketch, "E38.left", {"start": v(647.7, 2.54) * mm, "end": v(647.7, 22.86) * mm});
            skLineSegment(sketch, "E38.right", {"start": v(622.3, 2.54) * mm, "end": v(622.3, 22.86) * mm});
            skPoint(sketch, "E39.visualSharp", {"position": v(647.7, 25.4) * mm});
            skArc(sketch, "E39.filletArc", {"start": v(647.7, 22.86) * mm, "mid": v(646.96, 24.66) * mm, "end": v(645.16, 25.4) * mm});
            skPoint(sketch, "E40.visualSharp", {"position": v(647.7, 0) * mm});
            skArc(sketch, "E40.filletArc", {"start": v(645.16, 0) * mm, "mid": v(646.96, 0.74) * mm, "end": v(647.7, 2.54) * mm});
            skPoint(sketch, "E41.visualSharp", {"position": v(622.3, 0) * mm});
            skArc(sketch, "E41.filletArc", {"start": v(622.3, 2.54) * mm, "mid": v(623.04, 0.74) * mm, "end": v(624.84, 0) * mm});
            skPoint(sketch, "E42.visualSharp", {"position": v(622.3, 25.4) * mm});
            skArc(sketch, "E42.filletArc", {"start": v(624.84, 25.4) * mm, "mid": v(623.04, 24.66) * mm, "end": v(622.3, 22.86) * mm});
            skArc(sketch, "E43.0", {"start": v(646.56, 22.86) * mm, "mid": v(646.15, 23.85) * mm, "end": v(645.16, 24.26) * mm});
            skLineSegment(sketch, "E43.1", {"start": v(646.56, 2.54) * mm, "end": v(646.56, 22.86) * mm});
            skLineSegment(sketch, "E43.2", {"start": v(645.16, 24.26) * mm, "end": v(624.84, 24.26) * mm});
            skArc(sketch, "E43.3", {"start": v(645.16, 1.14) * mm, "mid": v(646.15, 1.55) * mm, "end": v(646.56, 2.54) * mm});
            skArc(sketch, "E43.4", {"start": v(624.84, 24.26) * mm, "mid": v(623.85, 23.85) * mm, "end": v(623.44, 22.86) * mm});
            skLineSegment(sketch, "E43.5", {"start": v(623.44, 2.54) * mm, "end": v(623.44, 22.86) * mm});
            skArc(sketch, "E43.6", {"start": v(623.44, 2.54) * mm, "mid": v(623.85, 1.55) * mm, "end": v(624.84, 1.14) * mm});
            skLineSegment(sketch, "E43.7", {"start": v(645.16, 1.14) * mm, "end": v(624.84, 1.14) * mm});
            skSolve(sketch);
        }
        {
            var Q0;
            Q0=qCreatedBy(id+"F21.planeOp",FACE);
            var sketch = newSketch(context, id + "F39", { "sketchPlane" : qUnion([Q0])});
            skLineSegment(sketch, "E44.0", {"start": v(645.16, 0) * mm, "end": v(624.84, 0) * mm});
            skLineSegment(sketch, "E44.1", {"start": v(645.16, 25.4) * mm, "end": v(624.84, 25.4) * mm});
            skLineSegment(sketch, "E44.2", {"start": v(647.7, 2.54) * mm, "end": v(647.7, 22.86) * mm});
            skLineSegment(sketch, "E44.3", {"start": v(622.3, 2.54) * mm, "end": v(622.3, 22.86) * mm});
            skPoint(sketch, "E44.4", {"position": v(647.7, 25.4) * mm});
            skArc(sketch, "E44.5", {"start": v(647.7, 22.86) * mm, "mid": v(646.96, 24.66) * mm, "end": v(645.16, 25.4) * mm});
            skPoint(sketch, "E44.6", {"position": v(647.7, 0) * mm});
            skArc(sketch, "E44.7", {"start": v(645.16, 0) * mm, "mid": v(646.96, 0.74) * mm, "end": v(647.7, 2.54) * mm});
            skPoint(sketch, "E44.8", {"position": v(622.3, 0) * mm});
            skArc(sketch, "E44.9", {"start": v(622.3, 2.54) * mm, "mid": v(623.04, 0.74) * mm, "end": v(624.84, 0) * mm});
            skPoint(sketch, "E44.10", {"position": v(622.3, 25.4) * mm});
            skArc(sketch, "E44.11", {"start": v(624.84, 25.4) * mm, "mid": v(623.04, 24.66) * mm, "end": v(622.3, 22.86) * mm});
            skArc(sketch, "E44.12", {"start": v(646.56, 22.86) * mm, "mid": v(646.15, 23.85) * mm, "end": v(645.16, 24.26) * mm});
            skLineSegment(sketch, "E44.13", {"start": v(646.56, 2.54) * mm, "end": v(646.56, 22.86) * mm});
            skLineSegment(sketch, "E44.14", {"start": v(645.16, 24.26) * mm, "end": v(624.84, 24.26) * mm});
            skArc(sketch, "E44.15", {"start": v(645.16, 1.14) * mm, "mid": v(646.15, 1.55) * mm, "end": v(646.56, 2.54) * mm});
            skArc(sketch, "E44.16", {"start": v(624.84, 24.26) * mm, "mid": v(623.85, 23.85) * mm, "end": v(623.44, 22.86) * mm});
            skLineSegment(sketch, "E44.17", {"start": v(623.44, 2.54) * mm, "end": v(623.44, 22.86) * mm});
            skArc(sketch, "E44.18", {"start": v(623.44, 2.54) * mm, "mid": v(623.85, 1.55) * mm, "end": v(624.84, 1.14) * mm});
            skLineSegment(sketch, "E44.19", {"start": v(645.16, 1.14) * mm, "end": v(624.84, 1.14) * mm});
            skSolve(sketch);
        }
        {
            var Q0;
            Q0 = qSketchRegion(id + "F39", true);
            var Q1;
            Q1=makeQuery(id+"F1.opExtrude","SWEPT_BODY",BODY,{"disambiguationData":[OSD([sQuery(id+"F0.wireOp",EDGE,"E0.bottom"),sQuery(id+"F0.wireOp",EDGE,"E0.top"),sQuery(id+"F0.wireOp",EDGE,"E0.left"),sQuery(id+"F0.wireOp",EDGE,"E0.right"),sQuery(id+"F0.wireOp",EDGE,"E1.filletArc"),sQuery(id+"F0.wireOp",EDGE,"E2.filletArc"),sQuery(id+"F0.wireOp",EDGE,"E3.filletArc"),sQuery(id+"F0.wireOp",EDGE,"E4.filletArc"),sQuery(id+"F0.wireOp",EDGE,"E5.0"),sQuery(id+"F0.wireOp",EDGE,"E5.1"),sQuery(id+"F0.wireOp",EDGE,"E5.2"),sQuery(id+"F0.wireOp",EDGE,"E5.3"),sQuery(id+"F0.wireOp",EDGE,"E5.4"),sQuery(id+"F0.wireOp",EDGE,"E5.5"),sQuery(id+"F0.wireOp",EDGE,"E5.6"),sQuery(id+"F0.wireOp",EDGE,"E6.0")])]});
            var Q2;
            Q2=makeQuery(id+"F4.opPattern","COPY",BODY,{"derivedFrom":makeQuery(id+"F1.opExtrude","SWEPT_BODY",BODY,{"disambiguationData":[OSD([sQuery(id+"F0.wireOp",EDGE,"E0.bottom"),sQuery(id+"F0.wireOp",EDGE,"E0.top"),sQuery(id+"F0.wireOp",EDGE,"E0.left"),sQuery(id+"F0.wireOp",EDGE,"E0.right"),sQuery(id+"F0.wireOp",EDGE,"E1.filletArc"),sQuery(id+"F0.wireOp",EDGE,"E2.filletArc"),sQuery(id+"F0.wireOp",EDGE,"E3.filletArc"),sQuery(id+"F0.wireOp",EDGE,"E4.filletArc"),sQuery(id+"F0.wireOp",EDGE,"E5.0"),sQuery(id+"F0.wireOp",EDGE,"E5.1"),sQuery(id+"F0.wireOp",EDGE,"E5.2"),sQuery(id+"F0.wireOp",EDGE,"E5.3"),sQuery(id+"F0.wireOp",EDGE,"E5.4"),sQuery(id+"F0.wireOp",EDGE,"E5.5"),sQuery(id+"F0.wireOp",EDGE,"E5.6"),sQuery(id+"F0.wireOp",EDGE,"E6.0")])]}),"instanceName":"1"});
            extrude(context, id + "F40", {"entities" : qUnion([Q0]), "endBound" : BoundingType.UP_TO_BODY, "endBoundEntityBody" : qUnion([Q1]), "depth" : 25.4 * mm, "hasSecondDirection" : true, "secondDirectionBound" : SecondDirectionBoundingType.UP_TO_BODY, "secondDirectionOppositeDirection" : true, "secondDirectionBoundEntityBody" : qUnion([Q2]), "secondDirectionDepth" : 25.4 * mm});
        }
        {
            var Q0;
            Q0=makeQuery(id+"F40.opExtrude","SWEPT_BODY",BODY,{"disambiguationData":[OSD([sQuery(id+"F39.wireOp",EDGE,"E44.0"),sQuery(id+"F39.wireOp",EDGE,"E44.1"),sQuery(id+"F39.wireOp",EDGE,"E44.2"),sQuery(id+"F39.wireOp",EDGE,"E44.3"),sQuery(id+"F39.wireOp",EDGE,"E44.5"),sQuery(id+"F39.wireOp",EDGE,"E44.7"),sQuery(id+"F39.wireOp",EDGE,"E44.9"),sQuery(id+"F39.wireOp",EDGE,"E44.11"),sQuery(id+"F39.wireOp",EDGE,"E44.12"),sQuery(id+"F39.wireOp",EDGE,"E44.13"),sQuery(id+"F39.wireOp",EDGE,"E44.14"),sQuery(id+"F39.wireOp",EDGE,"E44.15"),sQuery(id+"F39.wireOp",EDGE,"E44.16"),sQuery(id+"F39.wireOp",EDGE,"E44.17"),sQuery(id+"F39.wireOp",EDGE,"E44.18"),sQuery(id+"F39.wireOp",EDGE,"E44.19")])]});
            transform(context, id + "F41", {"entities" : qUnion([Q0]), "transformType" : TransformType.TRANSLATION_3D, "dx" : 0 * mm, "dy" : 0 * mm, "dz" : 304.8 * mm, "makeCopy" : true});
        }
        {
            var Q0;
            Q0=makeQuery(id+"F41.opPattern","COPY",BODY,{"derivedFrom":makeQuery(id+"F40.opExtrude","SWEPT_BODY",BODY,{"disambiguationData":[OSD([sQuery(id+"F39.wireOp",EDGE,"E44.0"),sQuery(id+"F39.wireOp",EDGE,"E44.1"),sQuery(id+"F39.wireOp",EDGE,"E44.2"),sQuery(id+"F39.wireOp",EDGE,"E44.3"),sQuery(id+"F39.wireOp",EDGE,"E44.5"),sQuery(id+"F39.wireOp",EDGE,"E44.7"),sQuery(id+"F39.wireOp",EDGE,"E44.9"),sQuery(id+"F39.wireOp",EDGE,"E44.11"),sQuery(id+"F39.wireOp",EDGE,"E44.12"),sQuery(id+"F39.wireOp",EDGE,"E44.13"),sQuery(id+"F39.wireOp",EDGE,"E44.14"),sQuery(id+"F39.wireOp",EDGE,"E44.15"),sQuery(id+"F39.wireOp",EDGE,"E44.16"),sQuery(id+"F39.wireOp",EDGE,"E44.17"),sQuery(id+"F39.wireOp",EDGE,"E44.18"),sQuery(id+"F39.wireOp",EDGE,"E44.19")])]}),"instanceName":"1"});
            transform(context, id + "F42", {"entities" : qUnion([Q0]), "transformType" : TransformType.TRANSLATION_3D, "dx" : 0 * mm, "dy" : 0 * mm, "dz" : 304.8 * mm, "makeCopy" : true});
        }
        {
            var Q0;
            Q0=qCreatedBy(id+"F37.planeOp",FACE);
            cPlane(context, id + "F43", {"entities" : qUnion([Q0]), "cplaneType" : CPlaneType.OFFSET, "offset" : 254 * mm, "width" : 152.4 * mm, "height" : 152.4 * mm});
        }
        {
            var Q0;
            Q0=qCreatedBy(id+"F43.planeOp",FACE);
            var sketch = newSketch(context, id + "F44", { "sketchPlane" : qUnion([Q0])});
            skLineSegment(sketch, "E45.bottom", {"start": v(31.75, 22.86) * mm, "end": v(57.15, 22.86) * mm});
            skLineSegment(sketch, "E45.top", {"start": v(31.75, 25.4) * mm, "end": v(57.15, 25.4) * mm});
            skLineSegment(sketch, "E45.left", {"start": v(31.75, 22.86) * mm, "end": v(31.75, 25.4) * mm});
            skLineSegment(sketch, "E45.right", {"start": v(57.15, 22.86) * mm, "end": v(57.15, 25.4) * mm});
            skSolve(sketch);
        }
        {
            var Q0;
            Q0 = qSketchRegion(id + "F44", true);
            var Q1;
            Q1=makeQuery(id+"F32.opPattern","COPY",BODY,{"derivedFrom":makeQuery(id+"F31.opExtrude","SWEPT_BODY",BODY,{"disambiguationData":[OSD([sQuery(id+"F30.wireOp",EDGE,"E37.bottom"),sQuery(id+"F30.wireOp",EDGE,"E37.top"),sQuery(id+"F30.wireOp",EDGE,"E37.left"),sQuery(id+"F30.wireOp",EDGE,"E37.right")])]}),"instanceName":"1"});
            var Q2;
            Q2=makeQuery(id+"F40.opExtrude","SWEPT_BODY",BODY,{"disambiguationData":[OSD([sQuery(id+"F39.wireOp",EDGE,"E44.0"),sQuery(id+"F39.wireOp",EDGE,"E44.1"),sQuery(id+"F39.wireOp",EDGE,"E44.2"),sQuery(id+"F39.wireOp",EDGE,"E44.3"),sQuery(id+"F39.wireOp",EDGE,"E44.5"),sQuery(id+"F39.wireOp",EDGE,"E44.7"),sQuery(id+"F39.wireOp",EDGE,"E44.9"),sQuery(id+"F39.wireOp",EDGE,"E44.11"),sQuery(id+"F39.wireOp",EDGE,"E44.12"),sQuery(id+"F39.wireOp",EDGE,"E44.13"),sQuery(id+"F39.wireOp",EDGE,"E44.14"),sQuery(id+"F39.wireOp",EDGE,"E44.15"),sQuery(id+"F39.wireOp",EDGE,"E44.16"),sQuery(id+"F39.wireOp",EDGE,"E44.17"),sQuery(id+"F39.wireOp",EDGE,"E44.18"),sQuery(id+"F39.wireOp",EDGE,"E44.19")])]});
            extrude(context, id + "F45", {"entities" : qUnion([Q0]), "endBound" : BoundingType.UP_TO_BODY, "endBoundEntityBody" : qUnion([Q1]), "depth" : 25.4 * mm, "hasSecondDirection" : true, "secondDirectionBound" : SecondDirectionBoundingType.UP_TO_BODY, "secondDirectionOppositeDirection" : true, "secondDirectionBoundEntityBody" : qUnion([Q2]), "secondDirectionDepth" : 25.4 * mm});
        }
        {
            var Q0;
            Q0=qCreatedBy(id+"F37.planeOp",FACE);
            cPlane(context, id + "F46", {"entities" : qUnion([Q0]), "cplaneType" : CPlaneType.OFFSET, "offset" : 254 * mm, "oppositeDirection" : true, "width" : 152.4 * mm, "height" : 152.4 * mm});
        }
        {
            var Q0;
            Q0=qCreatedBy(id+"F46.planeOp",FACE);
            var sketch = newSketch(context, id + "F47", { "sketchPlane" : qUnion([Q0])});
            skLineSegment(sketch, "E46.0", {"start": v(31.75, 22.86) * mm, "end": v(57.15, 22.86) * mm});
            skLineSegment(sketch, "E46.1", {"start": v(31.75, 25.4) * mm, "end": v(57.15, 25.4) * mm});
            skLineSegment(sketch, "E46.2", {"start": v(31.75, 22.86) * mm, "end": v(31.75, 25.4) * mm});
            skLineSegment(sketch, "E46.3", {"start": v(57.15, 22.86) * mm, "end": v(57.15, 25.4) * mm});
            skSolve(sketch);
        }
        {
            var Q0;
            Q0 = qSketchRegion(id + "F47", true);
            var Q1;
            Q1=makeQuery(id+"F40.opExtrude","SWEPT_BODY",BODY,{"disambiguationData":[OSD([sQuery(id+"F39.wireOp",EDGE,"E44.0"),sQuery(id+"F39.wireOp",EDGE,"E44.1"),sQuery(id+"F39.wireOp",EDGE,"E44.2"),sQuery(id+"F39.wireOp",EDGE,"E44.3"),sQuery(id+"F39.wireOp",EDGE,"E44.5"),sQuery(id+"F39.wireOp",EDGE,"E44.7"),sQuery(id+"F39.wireOp",EDGE,"E44.9"),sQuery(id+"F39.wireOp",EDGE,"E44.11"),sQuery(id+"F39.wireOp",EDGE,"E44.12"),sQuery(id+"F39.wireOp",EDGE,"E44.13"),sQuery(id+"F39.wireOp",EDGE,"E44.14"),sQuery(id+"F39.wireOp",EDGE,"E44.15"),sQuery(id+"F39.wireOp",EDGE,"E44.16"),sQuery(id+"F39.wireOp",EDGE,"E44.17"),sQuery(id+"F39.wireOp",EDGE,"E44.18"),sQuery(id+"F39.wireOp",EDGE,"E44.19")])]});
            var Q2;
            Q2=makeQuery(id+"F31.opExtrude","SWEPT_BODY",BODY,{"disambiguationData":[OSD([sQuery(id+"F30.wireOp",EDGE,"E37.bottom"),sQuery(id+"F30.wireOp",EDGE,"E37.top"),sQuery(id+"F30.wireOp",EDGE,"E37.left"),sQuery(id+"F30.wireOp",EDGE,"E37.right")])]});
            extrude(context, id + "F48", {"entities" : qUnion([Q0]), "endBound" : BoundingType.UP_TO_BODY, "endBoundEntityBody" : qUnion([Q1]), "depth" : 25.4 * mm, "hasSecondDirection" : true, "secondDirectionBound" : SecondDirectionBoundingType.UP_TO_BODY, "secondDirectionOppositeDirection" : true, "secondDirectionBoundEntityBody" : qUnion([Q2]), "secondDirectionDepth" : 25.4 * mm});
        }
        {
            var Q0;
            Q0=makeQuery(id+"F45.opExtrude","SWEPT_BODY",BODY,{"disambiguationData":[OSD([sQuery(id+"F44.wireOp",EDGE,"E45.bottom"),sQuery(id+"F44.wireOp",EDGE,"E45.top"),sQuery(id+"F44.wireOp",EDGE,"E45.left"),sQuery(id+"F44.wireOp",EDGE,"E45.right")])]});
            transform(context, id + "F49", {"entities" : qUnion([Q0]), "transformType" : TransformType.TRANSLATION_3D, "dx" : 0 * mm, "dy" : 450.85 * mm, "dz" : 0 * mm, "makeCopy" : true});
        }
        {
            var Q0;
            Q0=makeQuery(id+"F48.opExtrude","SWEPT_BODY",BODY,{"disambiguationData":[OSD([sQuery(id+"F47.wireOp",EDGE,"E46.0"),sQuery(id+"F47.wireOp",EDGE,"E46.1"),sQuery(id+"F47.wireOp",EDGE,"E46.2"),sQuery(id+"F47.wireOp",EDGE,"E46.3")])]});
            transform(context, id + "F50", {"entities" : qUnion([Q0]), "transformType" : TransformType.TRANSLATION_3D, "dx" : 0 * mm, "dy" : 450.85 * mm, "dz" : 0 * mm, "makeCopy" : true});
        }
        {
            var Q0;
            Q0=makeQuery(id+"F45.opExtrude","SWEPT_BODY",BODY,{"disambiguationData":[OSD([sQuery(id+"F44.wireOp",EDGE,"E45.bottom"),sQuery(id+"F44.wireOp",EDGE,"E45.top"),sQuery(id+"F44.wireOp",EDGE,"E45.left"),sQuery(id+"F44.wireOp",EDGE,"E45.right")])]});
            transform(context, id + "F51", {"entities" : qUnion([Q0]), "transformType" : TransformType.TRANSLATION_3D, "dx" : 0 * mm, "dy" : 0 * mm, "dz" : 304.8 * mm, "makeCopy" : true});
        }
        {
            var Q0;
            Q0=makeQuery(id+"F48.opExtrude","SWEPT_BODY",BODY,{"disambiguationData":[OSD([sQuery(id+"F47.wireOp",EDGE,"E46.0"),sQuery(id+"F47.wireOp",EDGE,"E46.1"),sQuery(id+"F47.wireOp",EDGE,"E46.2"),sQuery(id+"F47.wireOp",EDGE,"E46.3")])]});
            transform(context, id + "F52", {"entities" : qUnion([Q0]), "transformType" : TransformType.TRANSLATION_3D, "dx" : 0 * mm, "dy" : 0 * mm, "dz" : 304.8 * mm, "makeCopy" : true});
        }
        {
            var Q0;
            Q0=makeQuery(id+"F51.opPattern","COPY",BODY,{"derivedFrom":makeQuery(id+"F45.opExtrude","SWEPT_BODY",BODY,{"disambiguationData":[OSD([sQuery(id+"F44.wireOp",EDGE,"E45.bottom"),sQuery(id+"F44.wireOp",EDGE,"E45.top"),sQuery(id+"F44.wireOp",EDGE,"E45.left"),sQuery(id+"F44.wireOp",EDGE,"E45.right")])]}),"instanceName":"1"});
            transform(context, id + "F53", {"entities" : qUnion([Q0]), "transformType" : TransformType.TRANSLATION_3D, "dx" : 0 * mm, "dy" : 0 * mm, "dz" : 304.8 * mm, "makeCopy" : true});
        }
        {
            var Q0;
            Q0=makeQuery(id+"F52.opPattern","COPY",BODY,{"derivedFrom":makeQuery(id+"F48.opExtrude","SWEPT_BODY",BODY,{"disambiguationData":[OSD([sQuery(id+"F47.wireOp",EDGE,"E46.0"),sQuery(id+"F47.wireOp",EDGE,"E46.1"),sQuery(id+"F47.wireOp",EDGE,"E46.2"),sQuery(id+"F47.wireOp",EDGE,"E46.3")])]}),"instanceName":"1"});
            transform(context, id + "F54", {"entities" : qUnion([Q0]), "transformType" : TransformType.TRANSLATION_3D, "dx" : 0 * mm, "dy" : 0 * mm, "dz" : 304.8 * mm, "makeCopy" : true});
        }
        {
            var Q0;
            Q0=makeQuery(id+"F49.opPattern","COPY",BODY,{"derivedFrom":makeQuery(id+"F45.opExtrude","SWEPT_BODY",BODY,{"disambiguationData":[OSD([sQuery(id+"F44.wireOp",EDGE,"E45.bottom"),sQuery(id+"F44.wireOp",EDGE,"E45.top"),sQuery(id+"F44.wireOp",EDGE,"E45.left"),sQuery(id+"F44.wireOp",EDGE,"E45.right")])]}),"instanceName":"1"});
            transform(context, id + "F55", {"entities" : qUnion([Q0]), "transformType" : TransformType.TRANSLATION_3D, "dx" : 0 * mm, "dy" : 0 * mm, "dz" : 304.8 * mm, "makeCopy" : true});
        }
        {
            var Q0;
            Q0=makeQuery(id+"F50.opPattern","COPY",BODY,{"derivedFrom":makeQuery(id+"F48.opExtrude","SWEPT_BODY",BODY,{"disambiguationData":[OSD([sQuery(id+"F47.wireOp",EDGE,"E46.0"),sQuery(id+"F47.wireOp",EDGE,"E46.1"),sQuery(id+"F47.wireOp",EDGE,"E46.2"),sQuery(id+"F47.wireOp",EDGE,"E46.3")])]}),"instanceName":"1"});
            transform(context, id + "F56", {"entities" : qUnion([Q0]), "transformType" : TransformType.TRANSLATION_3D, "dx" : 0 * mm, "dy" : 0 * mm, "dz" : 304.8 * mm, "makeCopy" : true});
        }
        {
            var Q0;
            Q0=makeQuery(id+"F55.opPattern","COPY",BODY,{"derivedFrom":makeQuery(id+"F49.opPattern","COPY",BODY,{"derivedFrom":makeQuery(id+"F45.opExtrude","SWEPT_BODY",BODY,{"disambiguationData":[OSD([sQuery(id+"F44.wireOp",EDGE,"E45.bottom"),sQuery(id+"F44.wireOp",EDGE,"E45.top"),sQuery(id+"F44.wireOp",EDGE,"E45.left"),sQuery(id+"F44.wireOp",EDGE,"E45.right")])]}),"instanceName":"1"}),"instanceName":"1"});
            transform(context, id + "F57", {"entities" : qUnion([Q0]), "transformType" : TransformType.TRANSLATION_3D, "dx" : 0 * mm, "dy" : 0 * mm, "dz" : 304.8 * mm, "makeCopy" : true});
        }
        {
            var Q0;
            Q0=makeQuery(id+"F56.opPattern","COPY",BODY,{"derivedFrom":makeQuery(id+"F50.opPattern","COPY",BODY,{"derivedFrom":makeQuery(id+"F48.opExtrude","SWEPT_BODY",BODY,{"disambiguationData":[OSD([sQuery(id+"F47.wireOp",EDGE,"E46.0"),sQuery(id+"F47.wireOp",EDGE,"E46.1"),sQuery(id+"F47.wireOp",EDGE,"E46.2"),sQuery(id+"F47.wireOp",EDGE,"E46.3")])]}),"instanceName":"1"}),"instanceName":"1"});
            transform(context, id + "F58", {"entities" : qUnion([Q0]), "transformType" : TransformType.TRANSLATION_3D, "dx" : 0 * mm, "dy" : 0 * mm, "dz" : 304.8 * mm, "makeCopy" : true});
        }
        {
            var Q0;
            Q0=makeQuery(id+"F42.opPattern","COPY",FACE,{"derivedFrom":makeQuery(id+"F41.opPattern","COPY",FACE,{"derivedFrom":makeQuery(id+"F40.opExtrude","SWEPT_FACE",FACE,{"disambiguationData":[OSD([sQuery(id+"F39.wireOp",EDGE,"E44.1")])]}),"instanceName":"1"}),"instanceName":"1"});
            var sketch = newSketch(context, id + "F59", { "sketchPlane" : qUnion([Q0])});
            skLineSegment(sketch, "E47.0", {"start": v(1270, 508) * mm, "end": v(0, 508) * mm, "construction": true});
            skLineSegment(sketch, "E47.2", {"start": v(1270, 31.75) * mm, "end": v(0, 31.75) * mm, "construction": true});
            skLineSegment(sketch, "E47.3", {"start": v(0, 31.75) * mm, "end": v(0, 508) * mm, "construction": true});
            skPoint(sketch, "E48.orphan", {"position": v(0, 537.12) * mm});
            skPoint(sketch, "E47.1.end.orphan", {"position": v(1272.54, 539.66) * mm});
            skPoint(sketch, "E47.1.start.orphan", {"position": v(1272.54, 0.09) * mm});
            skPoint(sketch, "E49.orphan", {"position": v(0, 2.63) * mm});
            skLineSegment(sketch, "E50.0", {"start": v(1270, 31.75) * mm, "end": v(1270, 508) * mm, "construction": true});
            skPoint(sketch, "E51.orphan", {"position": v(1270, 537.12) * mm});
            skPoint(sketch, "E52.orphan", {"position": v(1270, 2.63) * mm});
            skLineSegment(sketch, "E53.0", {"start": v(1266.83, 504.82) * mm, "end": v(3.18, 504.82) * mm});
            skLineSegment(sketch, "E53.1", {"start": v(1266.83, 34.92) * mm, "end": v(1266.83, 504.82) * mm});
            skLineSegment(sketch, "E53.2", {"start": v(1266.83, 34.93) * mm, "end": v(3.18, 34.93) * mm});
            skLineSegment(sketch, "E53.3", {"start": v(3.18, 34.92) * mm, "end": v(3.18, 504.82) * mm});
            skSolve(sketch);
        }
        {
            var Q0;
            Q0 = qSketchRegion(id + "F59", true);
            extrude(context, id + "F60", {"entities" : qUnion([Q0]), "depth" : 6.35 * mm});
        }
        {
            var Q0;
            Q0=makeQuery(id+"F60.opExtrude","SWEPT_BODY",BODY,{"disambiguationData":[OSD([sQuery(id+"F59.wireOp",EDGE,"E53.0"),sQuery(id+"F59.wireOp",EDGE,"E53.1"),sQuery(id+"F59.wireOp",EDGE,"E53.2"),sQuery(id+"F59.wireOp",EDGE,"E53.3")])]});
            transform(context, id + "F61", {"entities" : qUnion([Q0]), "transformType" : TransformType.TRANSLATION_3D, "dx" : 0 * mm, "dy" : 0 * mm, "dz" : -304.8 * mm, "makeCopy" : true});
        }
        {
            var Q0;
            Q0=makeQuery(id+"F61.opPattern","COPY",BODY,{"derivedFrom":makeQuery(id+"F60.opExtrude","SWEPT_BODY",BODY,{"disambiguationData":[OSD([sQuery(id+"F59.wireOp",EDGE,"E53.0"),sQuery(id+"F59.wireOp",EDGE,"E53.1"),sQuery(id+"F59.wireOp",EDGE,"E53.2"),sQuery(id+"F59.wireOp",EDGE,"E53.3")])]}),"instanceName":"1"});
            transform(context, id + "F62", {"entities" : qUnion([Q0]), "transformType" : TransformType.TRANSLATION_3D, "dx" : 0 * mm, "dy" : 0 * mm, "dz" : -304.8 * mm, "makeCopy" : true});
        }
    });
